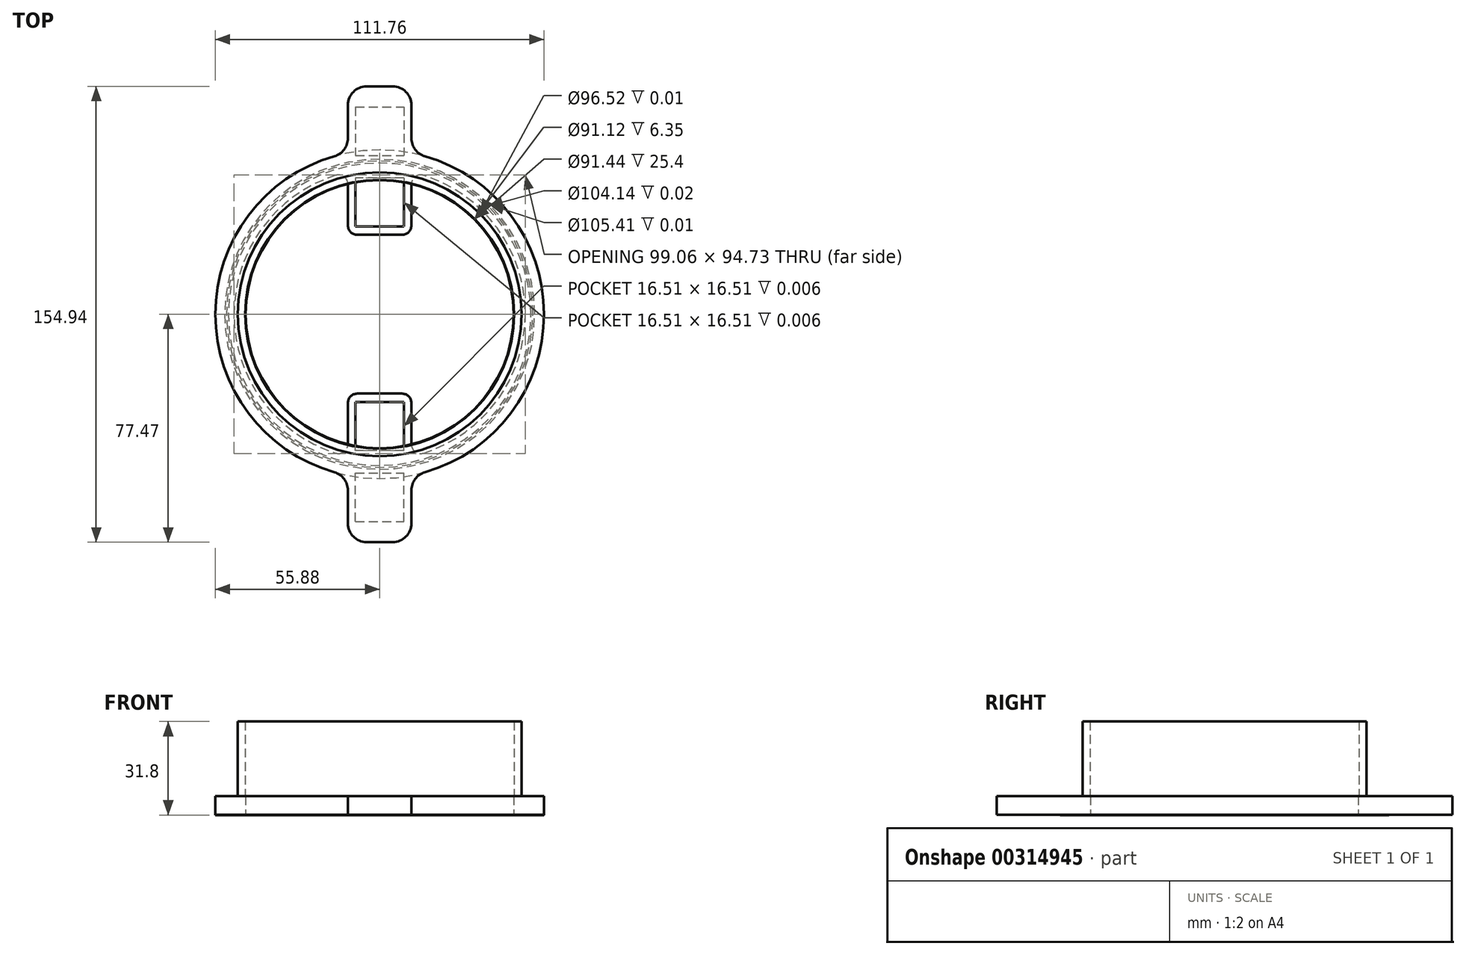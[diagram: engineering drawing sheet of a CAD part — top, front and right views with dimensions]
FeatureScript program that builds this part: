
annotation { "Feature Type Name" : "Feature", "Feature Type Description" : "" }
export const myFeature = defineFeature(function(context is Context, id is Id, definition is map)
    precondition{}
    {
        {
            var Q0;
            Q0=qCreatedBy(makeId("Top.planeOp"),FACE);
            var sketch = newSketch(context, id + "F0", { "sketchPlane" : qUnion([Q0])});
            skCircle(sketch, "E0", {"center": v(0, 0) * mm, "radius": 52.07 * mm});
            skCircle(sketch, "E1", {"center": v(0, 0) * mm, "radius": 55.88 * mm});
            skSolve(sketch);
        }
        {
            var Q0;
            Q0=qSketchRegion(id+"F0",true);
            extrude(context, id + "F1", {"entities" : qUnion([Q0]), "depth" : 1 / 50.8 * mm});
        }
        {
            var Q0;
            Q0=makeQuery(id+"F1.opExtrude","CAP_FACE",FACE,{"disambiguationData":[OSD([sQuery(id+"F0.wireOp",EDGE,"E0"),sQuery(id+"F0.wireOp",EDGE,"E1")])],"isStart":false});
            var sketch = newSketch(context, id + "F2", { "sketchPlane" : qUnion([Q0])});
            skCircle(sketch, "E2.0", {"center": v(0, 0) * mm, "radius": 55.88 * mm});
            skArc(sketch, "E3.0", {"start": v(-14.93, 47.23) * mm, "mid": v(-49.53, 0) * mm, "end": v(-14.93, -47.23) * mm});
            skPoint(sketch, "E4.middle", {"position": v(0, 43.18) * mm});
            skPoint(sketch, "E5.orphan", {"position": v(-12.07, 48.74) * mm});
            skPoint(sketch, "E6.orphan", {"position": v(10.8, 55.23) * mm});
            skLineSegment(sketch, "E7.MirrorCS", {"start": v(-10.8, -44.2) * mm, "end": v(-10.8, -30.16) * mm});
            skArc(sketch, "E8.trimOffspring", {"start": v(14.93, -47.23) * mm, "mid": v(49.53, 0) * mm, "end": v(14.93, 47.23) * mm});
            skPoint(sketch, "E9.visualSharp", {"position": v(-10.8, -48.34) * mm});
            skArc(sketch, "E9.filletArc", {"start": v(-14.93, -47.23) * mm, "mid": v(-12.1, -46.76) * mm, "end": v(-10.8, -44.2) * mm});
            skPoint(sketch, "E10.visualSharp", {"position": v(-10.8, -31.13) * mm});
            skPoint(sketch, "E11.visualSharp", {"position": v(12.06, -32.23) * mm});
            skPoint(sketch, "E12.visualSharp", {"position": v(21.27, -44.73) * mm});
            skPoint(sketch, "E13.visualSharp", {"position": v(-10.8, 31.13) * mm});
            skPoint(sketch, "E14.visualSharp", {"position": v(-10.8, 48.34) * mm});
            skPoint(sketch, "E15.visualSharp", {"position": v(21.27, 44.73) * mm});
            skLineSegment(sketch, "E16", {"start": v(7.62, -26.99) * mm, "end": v(-7.62, -26.99) * mm});
            skPoint(sketch, "E17.visualSharp", {"position": v(7.88, -26.99) * mm});
            skPoint(sketch, "E18.visualSharp", {"position": v(-10.8, -26.99) * mm});
            skArc(sketch, "E18.filletArc", {"start": v(-7.62, -26.99) * mm, "mid": v(-9.87, -27.92) * mm, "end": v(-10.8, -30.16) * mm});
            skLineSegment(sketch, "E19.MirrorCS", {"start": v(7.62, 26.99) * mm, "end": v(-7.62, 26.99) * mm});
            skArc(sketch, "E20.MirrorCS", {"start": v(-7.62, 26.99) * mm, "mid": v(-9.87, 27.92) * mm, "end": v(-10.8, 30.16) * mm});
            skLineSegment(sketch, "E21.MirrorCS", {"start": v(-10.8, 44.2) * mm, "end": v(-10.8, 30.16) * mm});
            skLineSegment(sketch, "E22.MirrorCS", {"start": v(10.8, 44.2) * mm, "end": v(10.8, 30.16) * mm});
            skArc(sketch, "E23.MirrorCS", {"start": v(7.62, 26.99) * mm, "mid": v(9.87, 27.92) * mm, "end": v(10.8, 30.16) * mm});
            skArc(sketch, "E24.MirrorCS", {"start": v(7.62, -26.99) * mm, "mid": v(9.87, -27.92) * mm, "end": v(10.8, -30.16) * mm});
            skLineSegment(sketch, "E25.MirrorCS", {"start": v(10.8, -44.2) * mm, "end": v(10.8, -30.16) * mm});
            skArc(sketch, "E26.MirrorCS", {"start": v(14.93, -47.23) * mm, "mid": v(12.1, -46.76) * mm, "end": v(10.8, -44.2) * mm});
            skPoint(sketch, "E27.orphan", {"position": v(5.08, 26.99) * mm});
            skPoint(sketch, "E28.orphan", {"position": v(5.08, -26.99) * mm});
            skArc(sketch, "E29.MirrorCS", {"start": v(-14.93, 47.23) * mm, "mid": v(-12.1, 46.76) * mm, "end": v(-10.8, 44.2) * mm});
            skArc(sketch, "E30.MirrorCS", {"start": v(14.93, 47.23) * mm, "mid": v(12.1, 46.76) * mm, "end": v(10.8, 44.2) * mm});
            skSolve(sketch);
        }
        {
            var Q0;
            Q0=qSketchRegion(id+"F2",true);
            extrude(context, id + "F3", {"entities" : qUnion([Q0]), "operationType" : NewBodyOperationType.ADD, "depth" : 1 / 101.6 * mm});
        }
        {
            var Q0;
            Q0=makeQuery(id+"F3.opExtrude","CAP_FACE",FACE,{"disambiguationData":[OSD([sQuery(id+"F2.wireOp",EDGE,"E2.0"),sQuery(id+"F2.wireOp",EDGE,"E3.0")])],"isStart":false});
            var sketch = newSketch(context, id + "F4", { "sketchPlane" : qUnion([Q0])});
            skCircle(sketch, "E31", {"center": v(0, 0) * mm, "radius": 52.7 * mm});
            skCircle(sketch, "E32.0", {"center": v(0, 0) * mm, "radius": 55.88 * mm});
            skSolve(sketch);
        }
        {
            var Q0;
            Q0=qSketchRegion(id+"F4",true);
            extrude(context, id + "F5", {"entities" : qUnion([Q0]), "operationType" : NewBodyOperationType.ADD, "depth" : 1 / 101.6 * mm});
        }
        {
            var Q0;
            Q0=makeQuery(id+"F3.opExtrude","CAP_FACE",FACE,{"disambiguationData":[OSD([sQuery(id+"F2.wireOp",EDGE,"E2.0"),sQuery(id+"F2.wireOp",EDGE,"E3.0"),sQuery(id+"F2.wireOp",EDGE,"E4.top"),sQuery(id+"F2.wireOp",EDGE,"E4.left"),sQuery(id+"F2.wireOp",EDGE,"E4.right"),sQuery(id+"F2.wireOp",EDGE,"E7.MirrorCS"),sQuery(id+"F2.wireOp",EDGE,"14d7e438-5bb9-4d8e-acd8-ebce0bf1a9fc0.MirrorCS"),sQuery(id+"F2.wireOp",EDGE,"57ccc243-d271-415f-816b-320263d1c3790.MirrorCS"),sQuery(id+"F2.wireOp",EDGE,"E8.trimOffspring"),sQuery(id+"F2.wireOp",EDGE,"E9.filletArc"),sQuery(id+"F2.wireOp",EDGE,"E10.filletArc"),sQuery(id+"F2.wireOp",EDGE,"E11.filletArc"),sQuery(id+"F2.wireOp",EDGE,"E12.filletArc"),sQuery(id+"F2.wireOp",EDGE,"E13.filletArc"),sQuery(id+"F2.wireOp",EDGE,"E14.filletArc"),sQuery(id+"F2.wireOp",EDGE,"E15.filletArc"),sQuery(id+"F2.wireOp",EDGE,"87325a1d-47ca-4d5e-9cd2-0e4b37ab90e0.filletArc")])],"isStart":false});
            var sketch = newSketch(context, id + "F6", { "sketchPlane" : qUnion([Q0])});
            skLineSegment(sketch, "E33.bottom", {"start": v(8.25, 46.35) * mm, "end": v(-8.26, 46.35) * mm});
            skLineSegment(sketch, "E33.top", {"start": v(8.25, 29.84) * mm, "end": v(-8.26, 29.84) * mm});
            skLineSegment(sketch, "E33.left", {"start": v(8.25, 46.35) * mm, "end": v(8.25, 29.84) * mm});
            skLineSegment(sketch, "E33.right", {"start": v(-8.26, 46.35) * mm, "end": v(-8.26, 29.84) * mm});
            skPoint(sketch, "E33.middle", {"position": v(0, 38.1) * mm});
            skLineSegment(sketch, "E34.MirrorCS", {"start": v(-8.26, -46.35) * mm, "end": v(-8.26, -29.84) * mm});
            skLineSegment(sketch, "E35.MirrorCS", {"start": v(8.25, -46.35) * mm, "end": v(8.25, -29.84) * mm});
            skLineSegment(sketch, "E36.MirrorCS", {"start": v(8.25, -29.84) * mm, "end": v(-8.26, -29.84) * mm});
            skLineSegment(sketch, "E37.MirrorCS", {"start": v(8.25, -46.35) * mm, "end": v(-8.26, -46.35) * mm});
            skPoint(sketch, "E38.MirrorP", {"position": v(0, -38.1) * mm});
            skSolve(sketch);
        }
        {
            var Q0;
            Q0=qSketchRegion(id+"F6",true);
            extrude(context, id + "F7", {"entities" : qUnion([Q0]), "operationType" : NewBodyOperationType.REMOVE, "oppositeDirection" : true, "depth" : 1 / 152.4 * mm});
        }
        {
            var Q0;
            Q0=makeQuery(id+"F5.opExtrude","CAP_FACE",FACE,{"disambiguationData":[OSD([sQuery(id+"F4.wireOp",EDGE,"E31"),sQuery(id+"F4.wireOp",EDGE,"E32.0")])],"isStart":false});
            var sketch = newSketch(context, id + "F8", { "sketchPlane" : qUnion([Q0])});
            skCircle(sketch, "E39.0", {"center": v(0, 0) * mm, "radius": 51.44 * mm});
            skPoint(sketch, "E40.visualSharp", {"position": v(-10.8, -26.99) * mm});
            skPoint(sketch, "E41.visualSharp", {"position": v(10.8, -26.99) * mm});
            skPoint(sketch, "E42.visualSharp", {"position": v(10.8, 26.99) * mm});
            skPoint(sketch, "E43.visualSharp", {"position": v(-10.8, 26.99) * mm});
            skArc(sketch, "E44", {"start": v(14.04, 46.17) * mm, "mid": v(-48.25, -0.98) * mm, "end": v(15.9, -45.56) * mm});
            skPoint(sketch, "E45.orphan", {"position": v(-10.8, -41.36) * mm});
            skPoint(sketch, "E46.orphan", {"position": v(10.8, -41.77) * mm});
            skArc(sketch, "E47.trimOffspring", {"start": v(15.9, -45.56) * mm, "mid": v(48.25, 0.98) * mm, "end": v(14.04, 46.17) * mm});
            skPoint(sketch, "E48.visualSharp", {"position": v(-11.43, -46.89) * mm});
            skPoint(sketch, "E49.visualSharp", {"position": v(11.43, -46.89) * mm});
            skPoint(sketch, "E50.orphan", {"position": v(-10.8, 41.36) * mm});
            skPoint(sketch, "E51.MirrorCS.start.orphan", {"position": v(10.8, 41.77) * mm});
            skSolve(sketch);
        }
        {
            var Q0;
            Q0=qSketchRegion(id+"F8",true);
            extrude(context, id + "F9", {"entities" : qUnion([Q0]), "operationType" : NewBodyOperationType.ADD, "depth" : 1 / 101.6 * mm});
        }
        {
            var Q0;
            Q0=makeQuery(id+"F9.opExtrude","CAP_FACE",FACE,{"disambiguationData":[OSD([sQuery(id+"F8.wireOp",EDGE,"E39.0"),sQuery(id+"F8.wireOp",EDGE,"c847aeb2-9136-4829-be3b-061b280800d2.0"),sQuery(id+"F8.wireOp",EDGE,"c847aeb2-9136-4829-be3b-061b280800d2.1"),sQuery(id+"F8.wireOp",EDGE,"c847aeb2-9136-4829-be3b-061b280800d2.2"),sQuery(id+"F8.wireOp",EDGE,"c847aeb2-9136-4829-be3b-061b280800d2.3"),sQuery(id+"F8.wireOp",EDGE,"c847aeb2-9136-4829-be3b-061b280800d2.4"),sQuery(id+"F8.wireOp",EDGE,"c847aeb2-9136-4829-be3b-061b280800d2.5"),sQuery(id+"F8.wireOp",EDGE,"c847aeb2-9136-4829-be3b-061b280800d2.6"),sQuery(id+"F8.wireOp",EDGE,"c847aeb2-9136-4829-be3b-061b280800d2.7"),sQuery(id+"F8.wireOp",EDGE,"c847aeb2-9136-4829-be3b-061b280800d2.8"),sQuery(id+"F8.wireOp",EDGE,"c847aeb2-9136-4829-be3b-061b280800d2.9"),sQuery(id+"F8.wireOp",EDGE,"c847aeb2-9136-4829-be3b-061b280800d2.10"),sQuery(id+"F8.wireOp",EDGE,"c847aeb2-9136-4829-be3b-061b280800d2.11"),sQuery(id+"F8.wireOp",EDGE,"c847aeb2-9136-4829-be3b-061b280800d2.12"),sQuery(id+"F8.wireOp",EDGE,"c847aeb2-9136-4829-be3b-061b280800d2.13"),sQuery(id+"F8.wireOp",EDGE,"c847aeb2-9136-4829-be3b-061b280800d2.14"),sQuery(id+"F8.wireOp",EDGE,"c847aeb2-9136-4829-be3b-061b280800d2.15")])],"isStart":false});
            var sketch = newSketch(context, id + "F10", { "sketchPlane" : qUnion([Q0])});
            skArc(sketch, "E52", {"start": v(-15.4, 53.72) * mm, "mid": v(-55.88, 0) * mm, "end": v(-15.4, -53.72) * mm});
            skCircle(sketch, "E53", {"center": v(0, 0) * mm, "radius": 45.56 * mm});
            skLineSegment(sketch, "E54", {"start": v(-10.8, 59.82) * mm, "end": v(-10.8, 71.12) * mm});
            skLineSegment(sketch, "E55.MirrorCS", {"start": v(10.8, 59.82) * mm, "end": v(10.8, 71.12) * mm});
            skLineSegment(sketch, "E56", {"start": v(-4.45, 77.47) * mm, "end": v(4.45, 77.47) * mm});
            skPoint(sketch, "E57.orphan", {"position": v(-10.8, 70.85) * mm});
            skPoint(sketch, "E58.orphan", {"position": v(-10.8, 49.27) * mm});
            skPoint(sketch, "E59.orphan", {"position": v(10.8, 49.27) * mm});
            skPoint(sketch, "E60.orphan", {"position": v(10.8, 70.85) * mm});
            skLineSegment(sketch, "E61.MirrorCS", {"start": v(-10.8, -59.82) * mm, "end": v(-10.8, -71.12) * mm});
            skLineSegment(sketch, "E62.MirrorCS", {"start": v(-4.44, -77.47) * mm, "end": v(4.45, -77.47) * mm});
            skLineSegment(sketch, "E63.MirrorCS", {"start": v(10.8, -59.82) * mm, "end": v(10.8, -71.12) * mm});
            skArc(sketch, "E64.trimOffspring", {"start": v(15.4, -53.72) * mm, "mid": v(55.88, 0) * mm, "end": v(15.4, 53.72) * mm});
            skPoint(sketch, "E65.visualSharp", {"position": v(10.8, 77.47) * mm});
            skArc(sketch, "E65.filletArc", {"start": v(10.8, 71.12) * mm, "mid": v(8.94, 75.61) * mm, "end": v(4.45, 77.47) * mm});
            skPoint(sketch, "E66.visualSharp", {"position": v(-10.8, 77.47) * mm});
            skArc(sketch, "E66.filletArc", {"start": v(-4.45, 77.47) * mm, "mid": v(-8.94, 75.61) * mm, "end": v(-10.8, 71.12) * mm});
            skPoint(sketch, "E67.visualSharp", {"position": v(10.8, 54.83) * mm});
            skArc(sketch, "E67.filletArc", {"start": v(10.8, 59.82) * mm, "mid": v(12.07, 56) * mm, "end": v(15.4, 53.72) * mm});
            skPoint(sketch, "E68.visualSharp", {"position": v(-10.8, 54.83) * mm});
            skArc(sketch, "E68.filletArc", {"start": v(-15.4, 53.72) * mm, "mid": v(-12.07, 56) * mm, "end": v(-10.8, 59.82) * mm});
            skPoint(sketch, "E69.visualSharp", {"position": v(10.8, -54.83) * mm});
            skArc(sketch, "E69.filletArc", {"start": v(15.4, -53.72) * mm, "mid": v(12.07, -56) * mm, "end": v(10.8, -59.82) * mm});
            skPoint(sketch, "E70.visualSharp", {"position": v(10.8, -77.47) * mm});
            skArc(sketch, "E70.filletArc", {"start": v(4.45, -77.47) * mm, "mid": v(8.94, -75.61) * mm, "end": v(10.8, -71.12) * mm});
            skPoint(sketch, "E71.visualSharp", {"position": v(-10.8, -77.47) * mm});
            skArc(sketch, "E71.filletArc", {"start": v(-10.8, -71.12) * mm, "mid": v(-8.94, -75.61) * mm, "end": v(-4.44, -77.47) * mm});
            skPoint(sketch, "E72.visualSharp", {"position": v(-10.8, -54.83) * mm});
            skArc(sketch, "E72.filletArc", {"start": v(-10.8, -59.82) * mm, "mid": v(-12.07, -56) * mm, "end": v(-15.4, -53.72) * mm});
            skSolve(sketch);
        }
        {
            var Q0;
            Q0=qSketchRegion(id+"F10",true);
            extrude(context, id + "F11", {"entities" : qUnion([Q0]), "operationType" : NewBodyOperationType.ADD, "depth" : 6.35 * mm});
        }
        {
            var Q0;
            Q0=makeQuery(id+"F11.opExtrude","CAP_FACE",FACE,{"disambiguationData":[OSD([sQuery(id+"F10.wireOp",EDGE,"E52"),sQuery(id+"F10.wireOp",EDGE,"E53")])],"isStart":false});
            var sketch = newSketch(context, id + "F12", { "sketchPlane" : qUnion([Q0])});
            skCircle(sketch, "E73", {"center": v(0, 0) * mm, "radius": 48.26 * mm});
            skCircle(sketch, "E74", {"center": v(0, 0) * mm, "radius": 45.72 * mm});
            skSolve(sketch);
        }
        {
            var Q0;
            Q0=qSketchRegion(id+"F12",true);
            extrude(context, id + "F13", {"entities" : qUnion([Q0]), "operationType" : NewBodyOperationType.ADD, "depth" : 25.4 * mm});
        }
        {
            var Q0;
            Q0=makeQuery(id+"F11.opExtrude","CAP_FACE",FACE,{"disambiguationData":[OSD([sQuery(id+"F10.wireOp",EDGE,"E52"),sQuery(id+"F10.wireOp",EDGE,"E53"),sQuery(id+"F10.wireOp",EDGE,"E54"),sQuery(id+"F10.wireOp",EDGE,"E55.MirrorCS"),sQuery(id+"F10.wireOp",EDGE,"E56"),sQuery(id+"F10.wireOp",EDGE,"E61.MirrorCS"),sQuery(id+"F10.wireOp",EDGE,"E62.MirrorCS"),sQuery(id+"F10.wireOp",EDGE,"E63.MirrorCS"),sQuery(id+"F10.wireOp",EDGE,"E64.trimOffspring")])],"isStart":true});
            var sketch = newSketch(context, id + "F14", { "sketchPlane" : qUnion([Q0])});
            skLineSegment(sketch, "E75.bottom", {"start": v(-8.26, -70.48) * mm, "end": v(8.26, -70.48) * mm});
            skLineSegment(sketch, "E75.top", {"start": v(-8.26, -53.98) * mm, "end": v(8.26, -53.98) * mm});
            skLineSegment(sketch, "E75.left", {"start": v(-8.26, -70.48) * mm, "end": v(-8.26, -53.98) * mm});
            skLineSegment(sketch, "E75.right", {"start": v(8.26, -70.48) * mm, "end": v(8.26, -53.98) * mm});
            skPoint(sketch, "E75.middle", {"position": v(0, -62.23) * mm});
            skPoint(sketch, "E75.middle.positionSnap0", {"position": v(10.8, -62.23) * mm});
            skPoint(sketch, "E75.centerSnap0", {"position": v(10.8, -62.23) * mm});
            skPoint(sketch, "E76.MirrorP", {"position": v(10.8, 62.23) * mm});
            skLineSegment(sketch, "E77.MirrorCS", {"start": v(8.25, 70.48) * mm, "end": v(8.25, 53.98) * mm});
            skLineSegment(sketch, "E78.MirrorCS", {"start": v(-8.26, 70.48) * mm, "end": v(-8.26, 53.98) * mm});
            skLineSegment(sketch, "E79.MirrorCS", {"start": v(-8.26, 53.98) * mm, "end": v(8.26, 53.98) * mm});
            skLineSegment(sketch, "E80.MirrorCS", {"start": v(-8.26, 70.48) * mm, "end": v(8.26, 70.48) * mm});
            skPoint(sketch, "E81.MirrorP", {"position": v(0, 62.23) * mm});
            skSolve(sketch);
        }
        {
            var Q0;
            Q0 = qSketchRegion(id + "F14", true);
            extrude(context, id + "F15", {"entities" : qUnion([Q0]), "operationType" : NewBodyOperationType.REMOVE, "oppositeDirection" : true, "depth" : 1 / 152.4 * mm});
        }
    });
